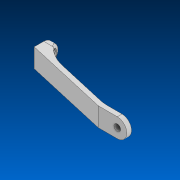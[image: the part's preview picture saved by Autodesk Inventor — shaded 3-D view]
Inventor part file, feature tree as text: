
AUTODESK INVENTOR PART (.ipt)
format: ipt  version: 2022.2 (Build 262287000, 287)  size: 159,232 bytes
history: native  units: in
note: dims shown in document units (in); Inventor stores cm internally (conversion verified against a paired STEP export)
features: sketch x3, fillet x2, hole x2, extrude x1, projected_geometry x1
ambient origin geometry x8: Origin, YZ Plane, XZ Plane, XY Plane, X Axis, Y Axis, Z Axis, Center Point
bodies: Solid1 (feature_tree)
feature tree (9):
  extrude  "Extrusion1"  Depth=1.0in
  fillet  "Fillet1"  Radius=0.125in
  fillet  "Fillet2"  Radius=1.0in
  hole  "Hole1"  [1 undecoded]
  hole  "Hole2"  [1 undecoded]
  sketch  "Sketch1"  dims[d0=0.125in d1=0.5in d2=0.125in d3=1.0in]
  sketch  "Sketch2"  dims[d4=3.1875in d5=1.0in]
  sketch  "Sketch3"  dims[d6=0.5in d7=0.0in d8=0.25in d12=0.175in d13=0.75in d14=0.35in d15=0.0in d16=0.5635in d17=1.0in d18=0.8108in d19=0.175in d20=0.75in d21=0.375in d22=0.25in d23=0.5635in d24=1.0in d25=0.8108in d26=0.25in d27=1.0in]
  projected_geometry  "Projected Loop1"
note: 2 required parameter values undecoded (feature->parameter linkage not recoverable at this tier; creation-order binding heuristic only, values carry confidence <= 0.55)
